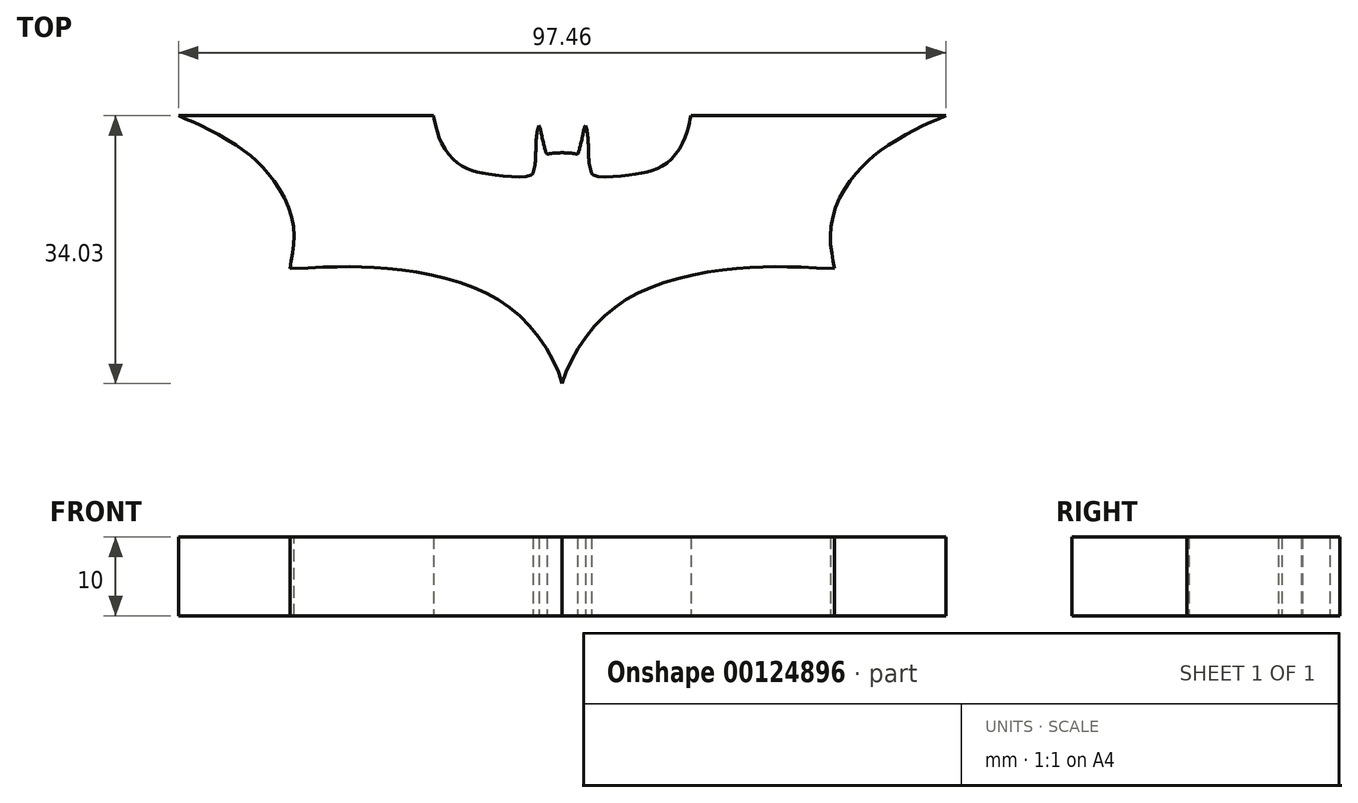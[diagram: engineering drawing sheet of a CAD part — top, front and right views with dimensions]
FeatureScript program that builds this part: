
annotation { "Feature Type Name" : "Feature", "Feature Type Description" : "" }
export const myFeature = defineFeature(function(context is Context, id is Id, definition is map)
    precondition{}
    {
        {
            var Q0;
            Q0=qCreatedBy(makeId("Top.planeOp"),FACE);
            var sketch = newSketch(context, id + "F0", { "sketchPlane" : qUnion([Q0])});
            skLineSegment(sketch, "E0", {"start": v(0, 49.83) * mm, "end": v(0, -55.17) * mm, "construction": true});
            skLineSegment(sketch, "E1", {"start": v(-65.13, 0) * mm, "end": v(97.42, 0) * mm, "construction": true});
            skFitSpline(sketch, "E2", {"points": [v(-34.57, -2.3) * mm, v(-24.17, -2.14) * mm, v(-13.27, -3.95) * mm, v(-4.72, -8.97) * mm, v(0, -16.9) * mm], "startDerivative": vector(56.76, 2.63) * mm, "endDerivative": vector(8.78, -32.22) * mm});
            skFitSpline(sketch, "E3", {"points": [v(-34.57, -2.3) * mm, v(-34.07, 1.25) * mm, v(-35, 6.12) * mm, v(-37.8, 10.3) * mm, v(-40.63, 12.84) * mm, v(-45.21, 15.56) * mm, v(-48.73, 17.13) * mm], "startDerivative": vector(2.48, 21.77) * mm, "endDerivative": vector(-20.98, 9.24) * mm});
            skLineSegment(sketch, "E4", {"start": v(-48.73, 17.13) * mm, "end": v(-16.34, 17.13) * mm});
            skFitSpline(sketch, "E5", {"points": [v(-16.34, 17.13) * mm, v(-16.1, 16.07) * mm, v(-15.36, 13.73) * mm, v(-13.35, 11.14) * mm, v(-11.16, 10.09) * mm, v(-8.1, 9.54) * mm, v(-4, 9.56) * mm, v(-3.71, 9.83) * mm], "startDerivative": vector(2, -9.91) * mm, "endDerivative": vector(-0.7, 0.7) * mm});
            skFitSpline(sketch, "E6", {"points": [v(-2.93, 15.9) * mm, v(-3.16, 15.12) * mm, v(-3.3, 13.96) * mm, v(-3.36, 12.08) * mm, v(-3.45, 11) * mm, v(-3.7, 9.82) * mm], "startDerivative": vector(-1.57, -4.6) * mm, "endDerivative": vector(-1.46, -6.12) * mm});
            skFitSpline(sketch, "E7", {"points": [v(-1.95, 12.25) * mm, v(-1.36, 12.34) * mm, v(-0.73, 12.4) * mm, v(0, 12.42) * mm], "startDerivative": vector(1.84, 0.3) * mm, "endDerivative": vector(2.1, 0) * mm});
            skFitSpline(sketch, "E8", {"points": [v(-2.93, 15.9) * mm, v(-2.79, 15.5) * mm, v(-2.6, 14.55) * mm, v(-2.32, 13.43) * mm, v(-2.12, 12.66) * mm, v(-1.95, 12.25) * mm], "startDerivative": vector(0.97, -2.36) * mm, "endDerivative": vector(1.15, -2.41) * mm});
            skFitSpline(sketch, "E9.MirrorCS", {"points": [v(1.95, 12.25) * mm, v(1.36, 12.34) * mm, v(0.73, 12.4) * mm, v(0, 12.42) * mm], "startDerivative": vector(-1.84, 0.3) * mm, "endDerivative": vector(-2.1, 0) * mm});
            skFitSpline(sketch, "E10.MirrorCS", {"points": [v(2.93, 15.9) * mm, v(2.79, 15.5) * mm, v(2.6, 14.55) * mm, v(2.32, 13.43) * mm, v(2.12, 12.66) * mm, v(1.95, 12.25) * mm], "startDerivative": vector(-0.97, -2.36) * mm, "endDerivative": vector(-1.15, -2.41) * mm});
            skFitSpline(sketch, "E11.MirrorCS", {"points": [v(2.93, 15.9) * mm, v(3.16, 15.12) * mm, v(3.3, 13.96) * mm, v(3.36, 12.08) * mm, v(3.45, 11) * mm, v(3.7, 9.82) * mm], "startDerivative": vector(1.57, -4.6) * mm, "endDerivative": vector(1.46, -6.12) * mm});
            skFitSpline(sketch, "E12.MirrorCS", {"points": [v(16.34, 17.13) * mm, v(16.1, 16.07) * mm, v(15.36, 13.73) * mm, v(13.35, 11.14) * mm, v(11.16, 10.09) * mm, v(8.1, 9.54) * mm, v(4, 9.56) * mm, v(3.71, 9.83) * mm], "startDerivative": vector(-2, -9.91) * mm, "endDerivative": vector(0.7, 0.7) * mm});
            skFitSpline(sketch, "E13.MirrorCS", {"points": [v(34.57, -2.3) * mm, v(34.07, 1.25) * mm, v(35, 6.12) * mm, v(37.8, 10.3) * mm, v(40.63, 12.84) * mm, v(45.21, 15.56) * mm, v(48.73, 17.13) * mm], "startDerivative": vector(-2.48, 21.77) * mm, "endDerivative": vector(20.98, 9.24) * mm});
            skFitSpline(sketch, "E14.MirrorCS", {"points": [v(34.57, -2.3) * mm, v(24.17, -2.14) * mm, v(13.27, -3.95) * mm, v(4.72, -8.97) * mm, v(0, -16.9) * mm], "startDerivative": vector(-56.76, 2.63) * mm, "endDerivative": vector(-8.78, -32.22) * mm});
            skLineSegment(sketch, "E15", {"start": v(3.72, 9.8) * mm, "end": v(3.7, 9.82) * mm});
            skLineSegment(sketch, "E16", {"start": v(-3.72, 9.8) * mm, "end": v(-3.7, 9.82) * mm});
            skLineSegment(sketch, "E17", {"start": v(16.34, 17.13) * mm, "end": v(48.73, 17.13) * mm});
            skSolve(sketch);
        }
        {
            var Q0;
            Q0 = qSketchRegion(id + "F0", true);
            extrude(context, id + "F1", {"entities" : qUnion([Q0]), "depth" : 10 * mm});
        }
    });
